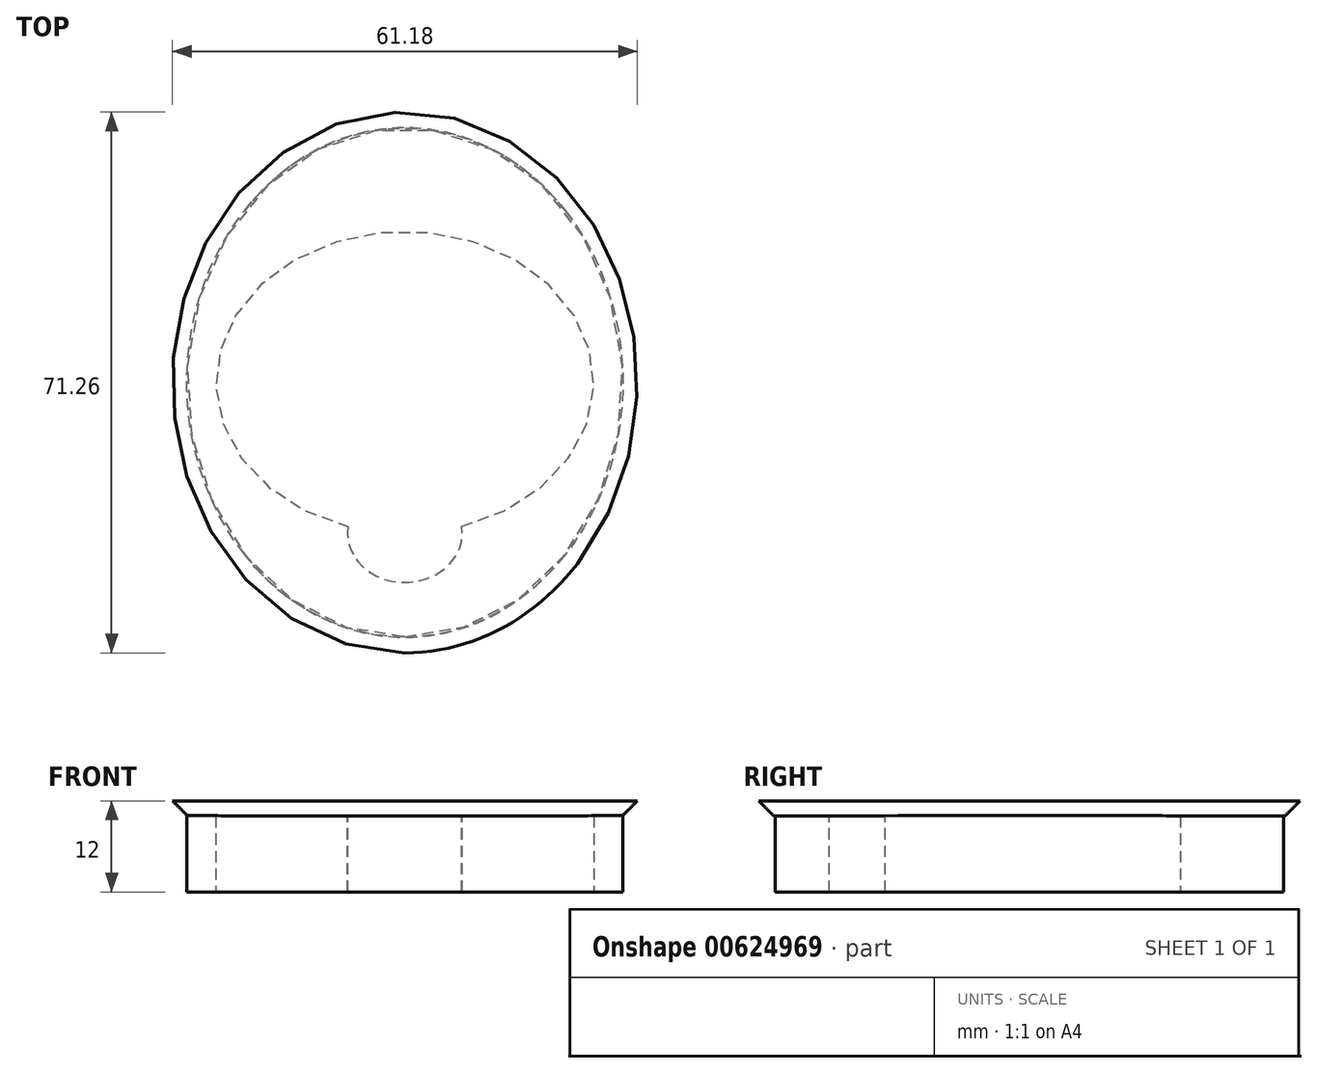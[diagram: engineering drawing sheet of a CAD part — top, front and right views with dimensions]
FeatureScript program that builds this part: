
annotation { "Feature Type Name" : "Feature", "Feature Type Description" : "" }
export const myFeature = defineFeature(function(context is Context, id is Id, definition is map)
    precondition{}
    {
        {
            var Q0;
            Q0=qCreatedBy(makeId("Top.planeOp"),FACE);
            var sketch = newSketch(context, id + "F0", { "sketchPlane" : qUnion([Q0])});
            skEllipse(sketch, "E0", {"center": v(0, 0) * mm, "majorRadius": 33.46 * mm, "minorRadius": 28.7 * mm, "majorAxis": v(0, -1)});
            skSolve(sketch);
        }
        {
            var Q0;
            Q0 = qSketchRegion(id + "F0", true);
            extrude(context, id + "F1", {"entities" : qUnion([Q0]), "depth" : 10 * mm, "offsetDistance" : 25 * mm});
        }
        {
            var Q0;
            Q0=makeQuery(id+"F1.opExtrude","CAP_FACE",FACE,{"disambiguationData":[OSD([sQuery(id+"F0.wireOp",EDGE,"E0")])],"isStart":false});
            var sketch = newSketch(context, id + "F2", { "sketchPlane" : qUnion([Q0])});
            skEllipse(sketch, "E1", {"center": v(0, 0) * mm, "majorRadius": 19.88 * mm, "minorRadius": 24.88 * mm, "majorAxis": v(0, -1)});
            skSolve(sketch);
        }
        {
            var Q0;
            Q0=makeQuery(id+"F2.imprint","IMPRINT",FACE,{"disambiguationData":[TD([[makeQuery(id+"F2.imprint","IMPRINT",EDGE,{"derivedFrom":sQuery(id+"F2.wireOp",EDGE,"E1")}),1.0]])]});
            extrude(context, id + "F3", {"entities" : qUnion([Q0]), "operationType" : NewBodyOperationType.REMOVE, "oppositeDirection" : true, "depth" : 20 * mm, "offsetDistance" : 25 * mm});
        }
        {
            var Q0;
            Q0=makeQuery(id+"F1.opExtrude","CAP_FACE",FACE,{"disambiguationData":[OSD([sQuery(id+"F0.wireOp",EDGE,"E0")])],"isStart":false});
            var sketch = newSketch(context, id + "F4", { "sketchPlane" : qUnion([Q0])});
            skEllipse(sketch, "E2", {"center": v(0, -19.88) * mm, "majorRadius": 6.47 * mm, "minorRadius": 7.56 * mm, "majorAxis": v(0, -1)});
            skSolve(sketch);
        }
        {
            var Q0;
            {var subQ0=sQuery(id+"F4.wireOp",EDGE,"E2");var subQ1=makeQuery(id+"F3.boolean.opBoolean","COPY",EDGE,{"derivedFrom":makeQuery(id+"F3.opExtrude","CAP_EDGE",EDGE,{"disambiguationData":[OSD([sQuery(id+"F2.wireOp",EDGE,"E1")])],"isStart":true})});var subQ2=makeQuery(id+"F4.imprint","INTERSECT",VERTEX,{"disambiguationData":[OD(0.0)],"derivedFrom":[subQ1,subQ0]});Q0=makeQuery(id+"F4.imprint","IMPRINT",FACE,{"disambiguationData":[TD([[makeQuery(id+"F4.imprint","IMPRINT",EDGE,{"disambiguationData":[TD([[subQ2,-1.0]])],"derivedFrom":subQ0}),1.0]])]});}
            extrude(context, id + "F5", {"entities" : qUnion([Q0]), "operationType" : NewBodyOperationType.REMOVE, "oppositeDirection" : true, "depth" : 20 * mm, "offsetDistance" : 25 * mm});
        }
        {
            var Q0;
            Q0=makeQuery(id+"F1.opExtrude","CAP_FACE",FACE,{"disambiguationData":[OSD([sQuery(id+"F0.wireOp",EDGE,"E0")])],"isStart":false});
            var sketch = newSketch(context, id + "F6", { "sketchPlane" : qUnion([Q0])});
            skEllipse(sketch, "E3", {"center": v(0, 0) * mm, "majorRadius": 36.13 * mm, "minorRadius": 31.1 * mm, "majorAxis": v(0, 1)});
            skSolve(sketch);
        }
        {
            var Q0;
            Q0 = qSketchRegion(id + "F6", true);
            extrude(context, id + "F7", {"entities" : qUnion([Q0]), "operationType" : NewBodyOperationType.ADD, "depth" : 2 * mm, "offsetDistance" : 25 * mm});
        }
        {
            var Q0;
            Q0=makeQuery(id+"F7.opExtrude","CAP_EDGE",EDGE,{"disambiguationData":[OSD([sQuery(id+"F6.wireOp",EDGE,"E3")])],"isStart":true});
            chamfer(context, id + "F8", {"entities" : qUnion([Q0]), "width" : 2.5 * mm, "tangentPropagation" : true});
        }
    });
